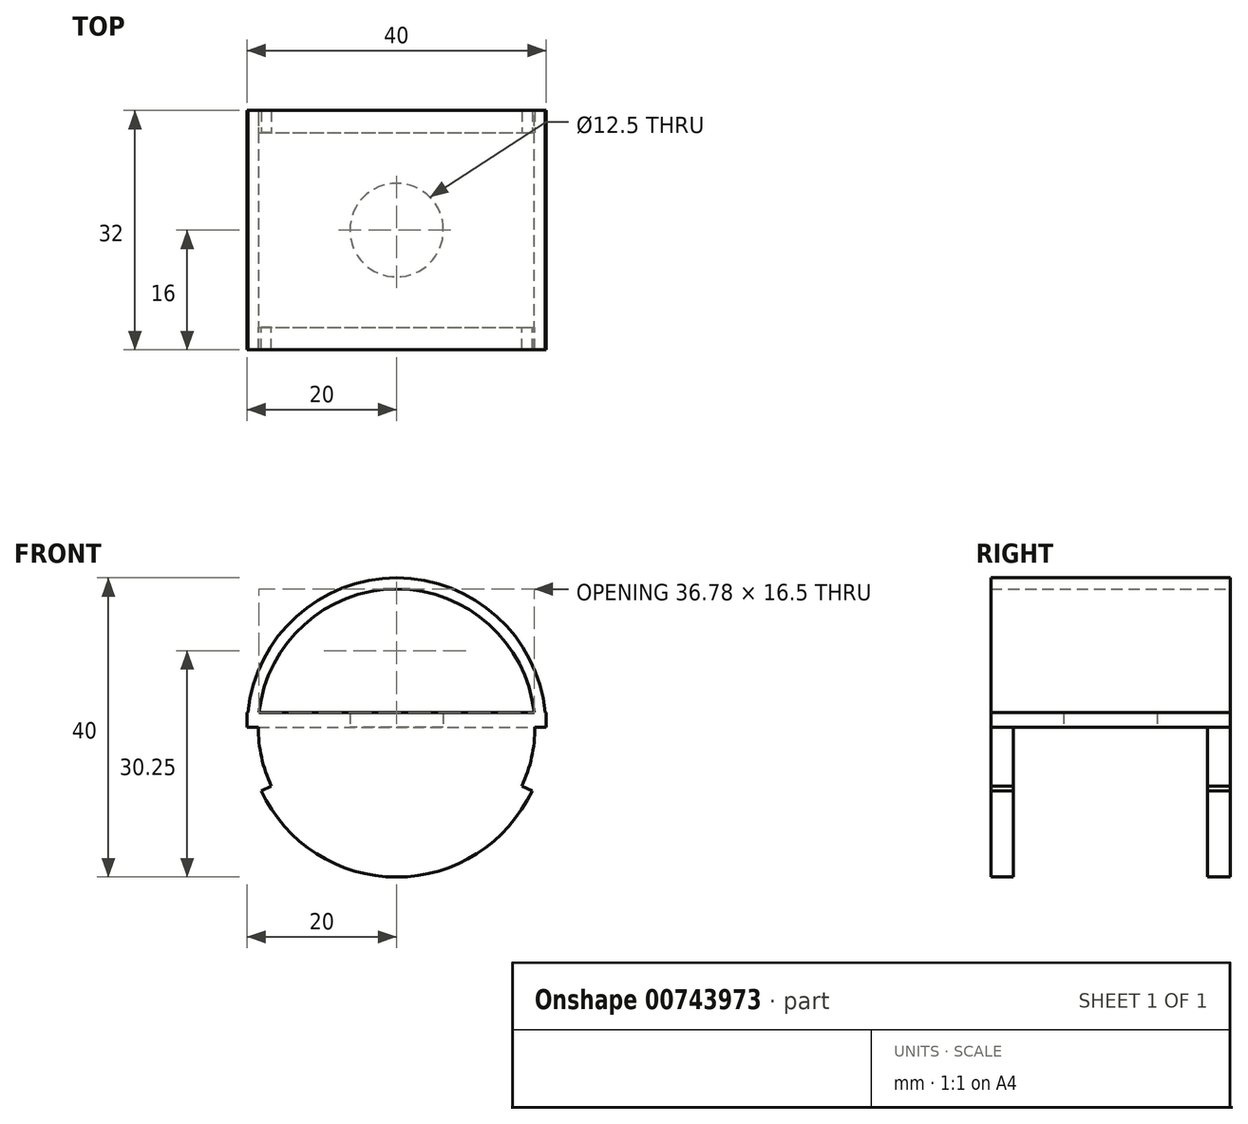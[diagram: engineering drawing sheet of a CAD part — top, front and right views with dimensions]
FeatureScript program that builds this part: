
annotation { "Feature Type Name" : "Feature", "Feature Type Description" : "" }
export const myFeature = defineFeature(function(context is Context, id is Id, definition is map)
    precondition{}
    {
        {
            var Q0;
            Q0=qCreatedBy(makeId("Top.planeOp"),FACE);
            var sketch = newSketch(context, id + "F0", { "sketchPlane" : qUnion([Q0])});
            skCircle(sketch, "E0", {"center": v(0, 0) * mm, "radius": 6.25 * mm});
            skLineSegment(sketch, "E1.bottom", {"start": v(20, 16) * mm, "end": v(-20, 16) * mm});
            skLineSegment(sketch, "E1.top", {"start": v(20, -16) * mm, "end": v(-20, -16) * mm});
            skLineSegment(sketch, "E1.left", {"start": v(20, 16) * mm, "end": v(20, -16) * mm});
            skLineSegment(sketch, "E1.right", {"start": v(-20, 16) * mm, "end": v(-20, -16) * mm});
            skSolve(sketch);
        }
        {
            var Q0;
            Q0 = qSketchRegion(id + "F0", true);
            extrude(context, id + "F1", {"entities" : qUnion([Q0]), "depth" : 2 * mm, "offsetDistance" : 25 * mm});
        }
        {
            var Q0;
            Q0=qCreatedBy(makeId("Front.planeOp"),FACE);
            var sketch = newSketch(context, id + "F2", { "sketchPlane" : qUnion([Q0])});
            skCircle(sketch, "E2", {"center": v(0, 0) * mm, "radius": 20 * mm});
            skLineSegment(sketch, "E3", {"start": v(-20, 0) * mm, "end": v(20, 0) * mm});
            skCircle(sketch, "E4", {"center": v(0, 0) * mm, "radius": 18.5 * mm});
            skLineSegment(sketch, "E5", {"start": v(0, 0) * mm, "end": v(-18.13, -8.45) * mm});
            skLineSegment(sketch, "E6", {"start": v(0, 0) * mm, "end": v(18.13, -8.45) * mm});
            skSolve(sketch);
        }
        {
            var Q0;
            {var subQ0=sQuery(id+"F2.wireOp",EDGE,"E3");Q0=makeQuery(id+"F2.imprint","IMPRINT",FACE,{"disambiguationData":[TD([[makeQuery(id+"F2.imprint","IMPRINT",EDGE,{"derivedFrom":subQ0}),-1.0]])]});}
            var Q1;
            {var subQ0=sQuery(id+"F2.wireOp",EDGE,"E3");var subQ1=sQuery(id+"F2.wireOp",EDGE,"E2");var subQ2=makeQuery(id+"F2.imprint","INTERSECT",VERTEX,{"disambiguationData":[OD(0.0)],"derivedFrom":[subQ1,subQ0]});Q1=makeQuery(id+"F2.imprint","IMPRINT",FACE,{"disambiguationData":[TD([[makeQuery(id+"F2.imprint","IMPRINT",EDGE,{"disambiguationData":[TD([[subQ2,-1.0]])],"derivedFrom":subQ1}),1.0]])]});}
            var Q2;
            {var subQ0=sQuery(id+"F2.wireOp",EDGE,"E5");var subQ1=sQuery(id+"F2.wireOp",EDGE,"E4");var subQ2=makeQuery(id+"F2.imprint","INTERSECT",VERTEX,{"derivedFrom":[subQ1,subQ0]});Q2=makeQuery(id+"F2.imprint","IMPRINT",FACE,{"disambiguationData":[TD([[makeQuery(id+"F2.imprint","IMPRINT",EDGE,{"disambiguationData":[TD([[subQ2,-1.0]])],"derivedFrom":subQ1}),1.0]])]});}
            var Q3;
            {var subQ0=sQuery(id+"F2.wireOp",EDGE,"E5");var subQ1=sQuery(id+"F2.wireOp",EDGE,"E2");var subQ2=makeQuery(id+"F2.imprint","INTERSECT",VERTEX,{"derivedFrom":[subQ1,subQ0]});Q3=makeQuery(id+"F2.imprint","IMPRINT",FACE,{"disambiguationData":[TD([[makeQuery(id+"F2.imprint","IMPRINT",EDGE,{"disambiguationData":[TD([[subQ2,-1.0]])],"derivedFrom":subQ1}),1.0]])]});}
            var Q4;
            {var subQ0=sQuery(id+"F2.wireOp",EDGE,"E3");var subQ1=sQuery(id+"F2.wireOp",EDGE,"E2");var subQ2=makeQuery(id+"F2.imprint","INTERSECT",VERTEX,{"disambiguationData":[OD(1.0)],"derivedFrom":[subQ1,subQ0]});Q4=makeQuery(id+"F2.imprint","IMPRINT",FACE,{"disambiguationData":[TD([[makeQuery(id+"F2.imprint","IMPRINT",EDGE,{"disambiguationData":[TD([[subQ2,1.0]])],"derivedFrom":subQ1}),1.0]])]});}
            extrude(context, id + "F3", {"entities" : qUnion([Q0, Q1, Q2, Q3, Q4]), "operationType" : NewBodyOperationType.ADD, "depth" : 16 * mm, "offsetDistance" : 25 * mm, "hasSecondDirection" : true, "secondDirectionOppositeDirection" : false, "secondDirectionDepth" : 13 * mm});
        }
        {
            var Q0;
            {var subQ0=sQuery(id+"F2.wireOp",EDGE,"E3");Q0=makeQuery(id+"F2.imprint","IMPRINT",FACE,{"disambiguationData":[TD([[makeQuery(id+"F2.imprint","IMPRINT",EDGE,{"derivedFrom":subQ0}),-1.0]])]});}
            var Q1;
            {var subQ0=sQuery(id+"F2.wireOp",EDGE,"E3");var subQ1=sQuery(id+"F2.wireOp",EDGE,"E2");var subQ2=makeQuery(id+"F2.imprint","INTERSECT",VERTEX,{"disambiguationData":[OD(0.0)],"derivedFrom":[subQ1,subQ0]});Q1=makeQuery(id+"F2.imprint","IMPRINT",FACE,{"disambiguationData":[TD([[makeQuery(id+"F2.imprint","IMPRINT",EDGE,{"disambiguationData":[TD([[subQ2,-1.0]])],"derivedFrom":subQ1}),1.0]])]});}
            var Q2;
            {var subQ0=sQuery(id+"F2.wireOp",EDGE,"E3");var subQ1=sQuery(id+"F2.wireOp",EDGE,"E2");var subQ2=makeQuery(id+"F2.imprint","INTERSECT",VERTEX,{"disambiguationData":[OD(1.0)],"derivedFrom":[subQ1,subQ0]});Q2=makeQuery(id+"F2.imprint","IMPRINT",FACE,{"disambiguationData":[TD([[makeQuery(id+"F2.imprint","IMPRINT",EDGE,{"disambiguationData":[TD([[subQ2,1.0]])],"derivedFrom":subQ1}),1.0]])]});}
            var Q3;
            {var subQ0=sQuery(id+"F2.wireOp",EDGE,"E5");var subQ1=sQuery(id+"F2.wireOp",EDGE,"E4");var subQ2=makeQuery(id+"F2.imprint","INTERSECT",VERTEX,{"derivedFrom":[subQ1,subQ0]});Q3=makeQuery(id+"F2.imprint","IMPRINT",FACE,{"disambiguationData":[TD([[makeQuery(id+"F2.imprint","IMPRINT",EDGE,{"disambiguationData":[TD([[subQ2,-1.0]])],"derivedFrom":subQ1}),1.0]])]});}
            var Q4;
            {var subQ0=sQuery(id+"F2.wireOp",EDGE,"E5");var subQ1=sQuery(id+"F2.wireOp",EDGE,"E2");var subQ2=makeQuery(id+"F2.imprint","INTERSECT",VERTEX,{"derivedFrom":[subQ1,subQ0]});Q4=makeQuery(id+"F2.imprint","IMPRINT",FACE,{"disambiguationData":[TD([[makeQuery(id+"F2.imprint","IMPRINT",EDGE,{"disambiguationData":[TD([[subQ2,-1.0]])],"derivedFrom":subQ1}),1.0]])]});}
            extrude(context, id + "F4", {"entities" : qUnion([Q0, Q1, Q2, Q3, Q4]), "operationType" : NewBodyOperationType.ADD, "oppositeDirection" : true, "depth" : 16 * mm, "offsetDistance" : 25 * mm, "hasSecondDirection" : true, "secondDirectionOppositeDirection" : true, "secondDirectionDepth" : 13 * mm});
        }
        {
            var Q0;
            {var subQ0=sQuery(id+"F2.wireOp",EDGE,"E3");var subQ1=sQuery(id+"F2.wireOp",EDGE,"E2");var subQ2=makeQuery(id+"F2.imprint","INTERSECT",VERTEX,{"disambiguationData":[OD(1.0)],"derivedFrom":[subQ1,subQ0]});Q0=makeQuery(id+"F2.imprint","IMPRINT",FACE,{"disambiguationData":[TD([[makeQuery(id+"F2.imprint","IMPRINT",EDGE,{"disambiguationData":[TD([[subQ2,1.0]])],"derivedFrom":subQ1}),1.0]])]});}
            var Q1;
            {var subQ0=sQuery(id+"F2.wireOp",EDGE,"E3");var subQ1=sQuery(id+"F2.wireOp",EDGE,"E2");var subQ2=makeQuery(id+"F2.imprint","INTERSECT",VERTEX,{"disambiguationData":[OD(0.0)],"derivedFrom":[subQ1,subQ0]});Q1=makeQuery(id+"F2.imprint","IMPRINT",FACE,{"disambiguationData":[TD([[makeQuery(id+"F2.imprint","IMPRINT",EDGE,{"disambiguationData":[TD([[subQ2,-1.0]])],"derivedFrom":subQ1}),1.0]])]});}
            extrude(context, id + "F5", {"entities" : qUnion([Q0, Q1]), "operationType" : NewBodyOperationType.ADD, "endBound" : BoundingType.SYMMETRIC, "depth" : 32 * mm, "offsetDistance" : 25 * mm});
        }
    });
